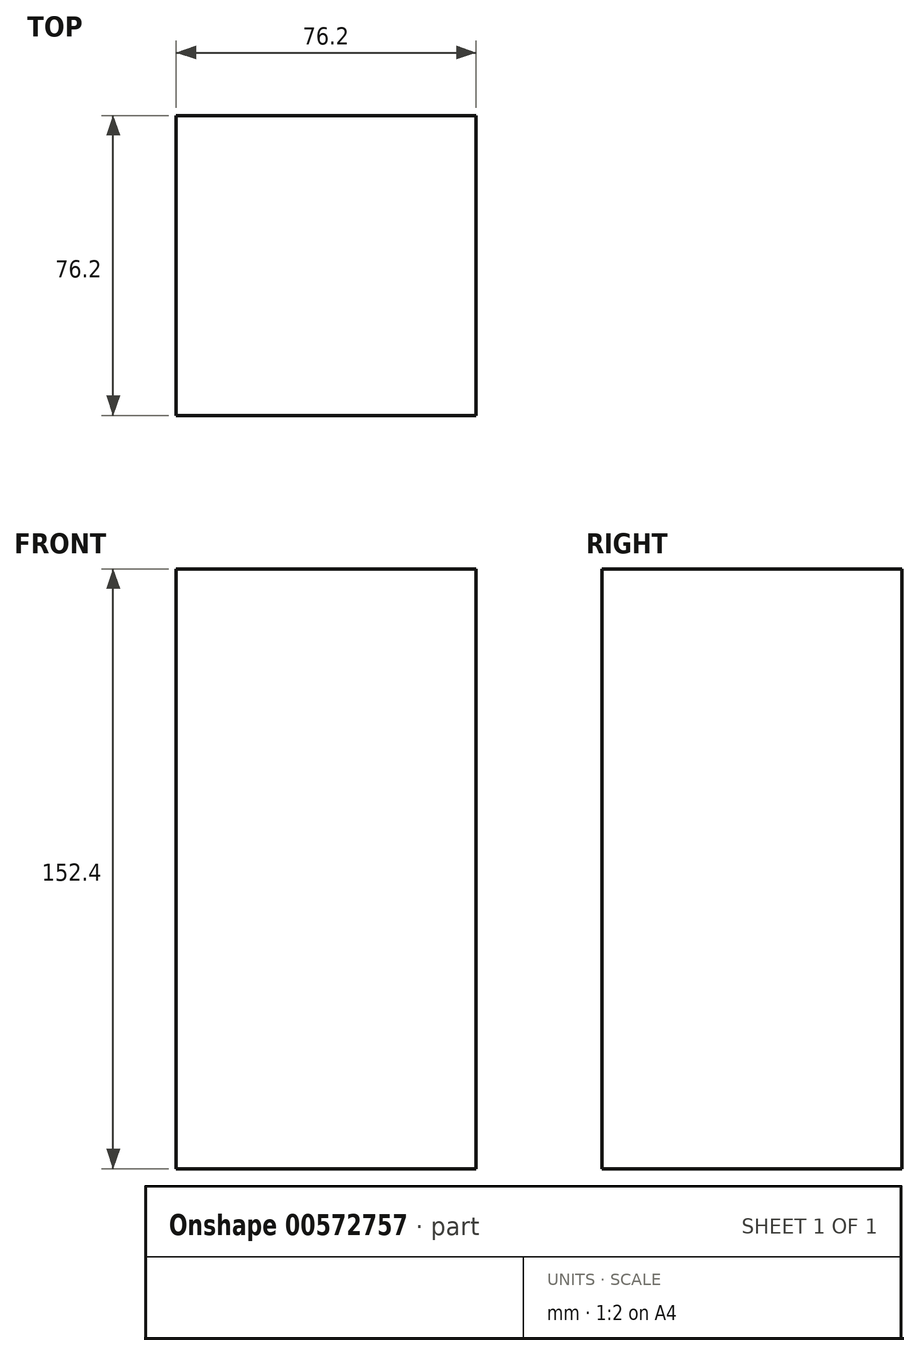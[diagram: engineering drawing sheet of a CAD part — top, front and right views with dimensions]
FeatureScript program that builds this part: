
annotation { "Feature Type Name" : "Feature", "Feature Type Description" : "" }
export const myFeature = defineFeature(function(context is Context, id is Id, definition is map)
    precondition{}
    {
        {
            var Q0;
            Q0=qCreatedBy(makeId("Front.planeOp"),FACE);
            var sketch = newSketch(context, id + "F0", { "sketchPlane" : qUnion([Q0])});
            skLineSegment(sketch, "E0.bottom", {"start": v(0, 0) * mm, "end": v(76.2, 0) * mm});
            skLineSegment(sketch, "E0.top", {"start": v(0, 152.4) * mm, "end": v(76.2, 152.4) * mm});
            skLineSegment(sketch, "E0.left", {"start": v(0, 0) * mm, "end": v(0, 152.4) * mm});
            skLineSegment(sketch, "E0.right", {"start": v(76.2, 0) * mm, "end": v(76.2, 152.4) * mm});
            skSolve(sketch);
        }
        {
            var Q0;
            Q0=makeQuery(id+"F0.imprint","IMPRINT",FACE,{"disambiguationData":[TD([[makeQuery(id+"F0.imprint","IMPRINT",EDGE,{"derivedFrom":sQuery(id+"F0.wireOp",EDGE,"E0.bottom")}),1.0]])]});
            extrude(context, id + "F1", {"entities" : qUnion([Q0]), "depth" : 76.2 * mm, "offsetDistance" : 25.4 * mm});
        }
    });
